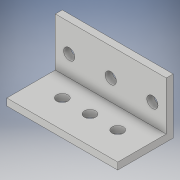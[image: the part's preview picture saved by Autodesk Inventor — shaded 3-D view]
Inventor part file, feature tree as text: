
AUTODESK INVENTOR PART (.ipt)
format: ipt  version: 2018 (Build 220112000, 112)  size: 134,144 bytes
history: native  units: in
note: dims shown in document units (in); Inventor stores cm internally (conversion verified against a paired STEP export)
features: extrude x3, sketch x3
ambient origin geometry x8: Origin, YZ Plane, XZ Plane, XY Plane, X Axis, Y Axis, Z Axis, Center Point
bodies: Solid1 (feature_tree)
feature tree (6):
  extrude  "Extrusion1"  Depth=1.0in
  extrude  "Extrusion2"  Depth=0.125in
  extrude  "Extrusion3"  Depth=2.0in
  sketch  "Sketch1"  dims[d0=0.125in d1=1.0in]
  sketch  "Sketch2"  dims[d2=0.875in d3=0.125in]
  sketch  "Sketch3"  dims[d4=2.0in d5=0.0in d6=0.5in d7=0.5in d8=0.2031in d9=0.2031in d10=0.2031in d11=2.0in d12=0.0in d19=2.0in d20=0.0in d22=0.5in d23=0.75in d24=0.75in d25=0.2031in d26=0.2031in d27=0.2031in]
